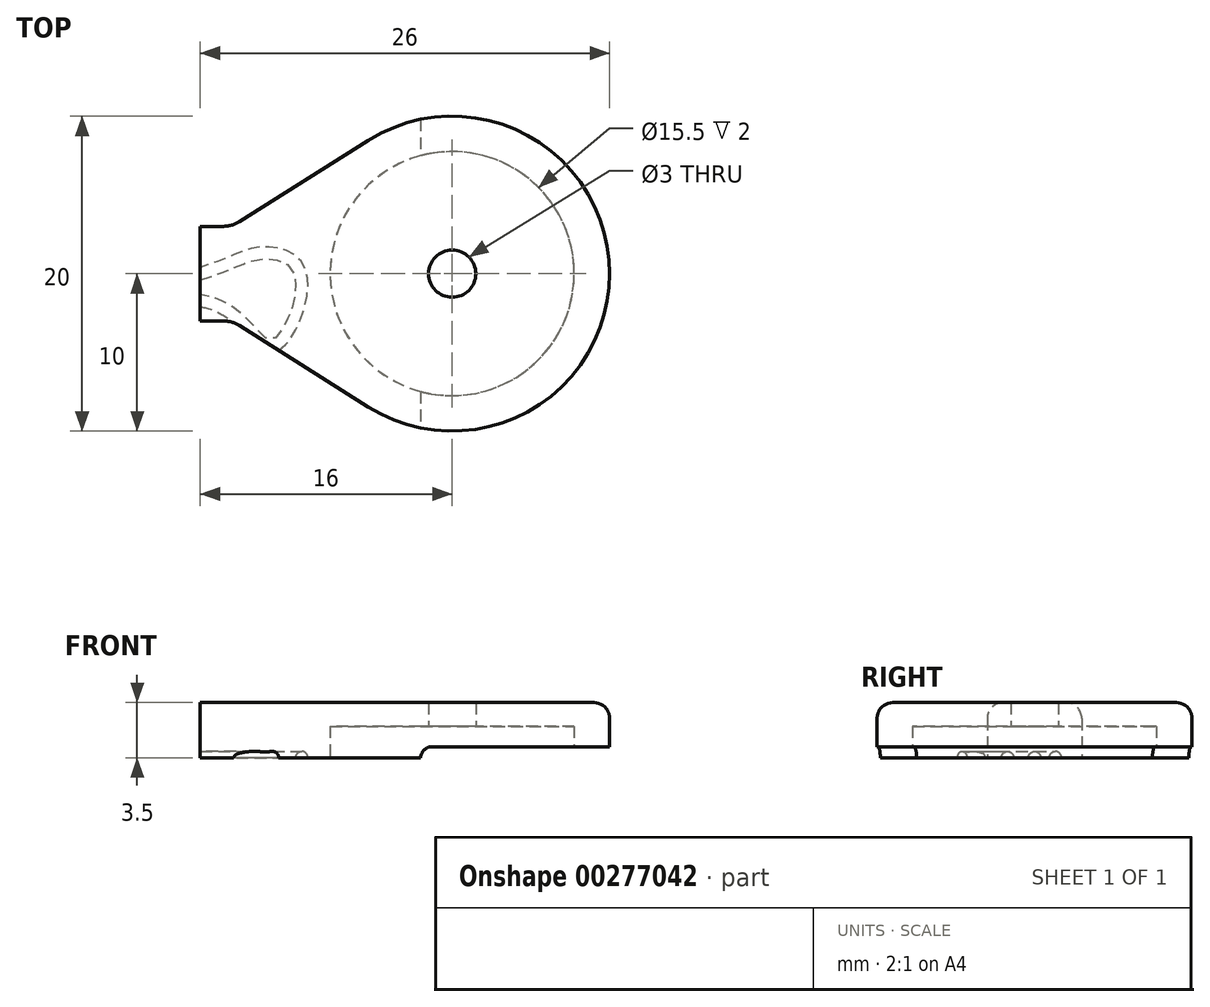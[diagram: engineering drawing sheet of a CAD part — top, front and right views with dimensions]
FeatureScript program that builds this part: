
annotation { "Feature Type Name" : "Feature", "Feature Type Description" : "" }
export const myFeature = defineFeature(function(context is Context, id is Id, definition is map)
    precondition{}
    {
        {
            var Q0;
            Q0=qCreatedBy(makeId("Top.planeOp"),FACE);
            var sketch = newSketch(context, id + "F0", { "sketchPlane" : qUnion([Q0])});
            skCircle(sketch, "E0", {"center": v(0, 0) * mm, "radius": 7.75 * mm});
            skCircle(sketch, "E1", {"center": v(0, 0) * mm, "radius": 10 * mm});
            skSolve(sketch);
        }
        {
            var Q0;
            Q0=qSketchRegion(id+"F0",true);
            extrude(context, id + "F1", {"entities" : qUnion([Q0]), "depth" : 2 * mm});
        }
        {
            var Q0;
            Q0=qCreatedBy(makeId("Top.planeOp"),FACE);
            var sketch = newSketch(context, id + "F2", { "sketchPlane" : qUnion([Q0])});
            skCircle(sketch, "E2.0", {"center": v(0, 0) * mm, "radius": 10 * mm});
            skCircle(sketch, "E3", {"center": v(0, 0) * mm, "radius": 1.5 * mm});
            skSolve(sketch);
        }
        {
            var Q0;
            Q0=qSketchRegion(id+"F2",true);
            extrude(context, id + "F3", {"entities" : qUnion([Q0]), "operationType" : NewBodyOperationType.ADD, "oppositeDirection" : true, "depth" : 1.5 * mm});
        }
        {
            var Q0;
            Q0=qCreatedBy(makeId("Top.planeOp"),FACE);
            var sketch = newSketch(context, id + "F4", { "sketchPlane" : qUnion([Q0])});
            skArc(sketch, "E4.0", {"start": v(-5.33, 8.46) * mm, "mid": v(-10, 0) * mm, "end": v(-5.33, -8.46) * mm});
            skLineSegment(sketch, "E5", {"start": v(-13.51, 3.3) * mm, "end": v(-5.33, 8.46) * mm});
            skLineSegment(sketch, "E6", {"start": v(-13.51, -3.3) * mm, "end": v(-5.33, -8.46) * mm});
            skLineSegment(sketch, "E7.bottom", {"start": v(-14.58, 3) * mm, "end": v(-16, 3) * mm});
            skLineSegment(sketch, "E7.top", {"start": v(-14.58, -3) * mm, "end": v(-16, -3) * mm});
            skLineSegment(sketch, "E7.right", {"start": v(-16, 3) * mm, "end": v(-16, -3) * mm});
            skPoint(sketch, "E8.orphan", {"position": v(-18.76, 0) * mm});
            skPoint(sketch, "E9.visualSharp", {"position": v(-14, 3) * mm});
            skArc(sketch, "E9.filletArc", {"start": v(-14.58, 3) * mm, "mid": v(-14.02, 3.08) * mm, "end": v(-13.51, 3.3) * mm});
            skPoint(sketch, "E10.visualSharp", {"position": v(-14, -3) * mm});
            skArc(sketch, "E10.filletArc", {"start": v(-13.51, -3.3) * mm, "mid": v(-14.02, -3.08) * mm, "end": v(-14.58, -3) * mm});
            skSolve(sketch);
        }
        {
            var Q0;
            Q0=qSketchRegion(id+"F4",true);
            var Q1;
            Q1=makeQuery(id+"F1.opExtrude","CAP_FACE",FACE,{"disambiguationData":[OSD([sQuery(id+"F0.wireOp",EDGE,"E0"),sQuery(id+"F0.wireOp",EDGE,"E1")])],"isStart":false});
            var Q2;
            Q2=makeQuery(id+"F3.opExtrude","CAP_FACE",FACE,{"disambiguationData":[OSD([sQuery(id+"F2.wireOp",EDGE,"E2.0"),sQuery(id+"F2.wireOp",EDGE,"E3")])],"isStart":false});
            extrude(context, id + "F5", {"entities" : qUnion([Q0]), "operationType" : NewBodyOperationType.ADD, "endBound" : BoundingType.UP_TO_SURFACE, "endBoundEntityFace" : qUnion([Q1]), "depth" : 25 * mm, "hasSecondDirection" : true, "secondDirectionBound" : BoundingType.UP_TO_SURFACE, "secondDirectionOppositeDirection" : true, "secondDirectionBoundEntityFace" : qUnion([Q2]), "secondDirectionDepth" : 25 * mm});
        }
        {
            var Q0;
            Q0=qCreatedBy(makeId("Front.planeOp"),FACE);
            var sketch = newSketch(context, id + "F6", { "sketchPlane" : qUnion([Q0])});
            skLineSegment(sketch, "E11", {"start": v(10.19, 2) * mm, "end": v(10.19, 1.3) * mm});
            skLineSegment(sketch, "E12", {"start": v(10.19, 1.3) * mm, "end": v(-1.3, 1.3) * mm});
            skArc(sketch, "E13", {"start": v(-1.3, 1.3) * mm, "mid": v(-1.8, 1.5) * mm, "end": v(-2, 2) * mm});
            skLineSegment(sketch, "E14", {"start": v(-2, 2) * mm, "end": v(10.19, 2) * mm});
            skSolve(sketch);
        }
        {
            var Q0;
            Q0=qSketchRegion(id+"F6",true);
            extrude(context, id + "F7", {"entities" : qUnion([Q0]), "operationType" : NewBodyOperationType.REMOVE, "oppositeDirection" : true, "depth" : 25 * mm, "hasSecondDirection" : true, "secondDirectionOppositeDirection" : false, "secondDirectionDepth" : 25 * mm});
        }
        {
            var Q0;
            {var subQ0=sQuery(id+"F0.wireOp",EDGE,"E1");var subQ1=sQuery(id+"F0.wireOp",EDGE,"E0");Q0=makeQuery(id+"F5.boolean.opBoolean","MERGE",FACE,{"derivedFrom":[makeQuery(id+"F1.opExtrude","CAP_FACE",FACE,{"disambiguationData":[OSD([subQ1,subQ0])],"isStart":false}),makeQuery(id+"F5.opExtrude","CAP_FACE",FACE,{"disambiguationData":[OSD([subQ1,subQ0])],"isStart":false})]});}
            var sketch = newSketch(context, id + "F8", { "sketchPlane" : qUnion([Q0])});
            skFitSpline(sketch, "E15", {"points": [v(-17.04, -0.28) * mm, v(-12.13, 1.31) * mm, v(-9.63, 0) * mm, v(-11.42, -4.62) * mm, v(-16.73, -1.68) * mm], "startDerivative": vector(32.92, 8.05) * mm, "endDerivative": vector(-35.55, -0.33) * mm});
            skSolve(sketch);
        }
        {
            var Q0;
            Q0=makeQuery(id+"F5.opExtrude","SWEPT_FACE",FACE,{"disambiguationData":[OSD([sQuery(id+"F4.wireOp",EDGE,"E7.right")])]});
            var sketch = newSketch(context, id + "F9", { "sketchPlane" : qUnion([Q0])});
            skCircle(sketch, "E16", {"center": v(0, 2) * mm, "radius": 0.4 * mm});
            skPoint(sketch, "E16.centerSnap0", {"position": v(0, 2) * mm});
            skSolve(sketch);
        }
        {
            var Q0;
            Q0=makeQuery(id+"F9.imprint","IMPRINT",FACE,{"disambiguationData":[TD([[makeQuery(id+"F9.imprint","IMPRINT",EDGE,{"derivedFrom":sQuery(id+"F9.wireOp",EDGE,"E16")}),1.0]])]});
            var Q1;
            Q1=qConstructionFilter(qBodyType(qCreatedBy(id+"F8",EDGE),BodyType.WIRE),ConstructionObject.NO);
            sweep(context, id + "F10", {"operationType" : NewBodyOperationType.REMOVE, "profiles" : qUnion([Q0]), "path" : qUnion([Q1])});
        }
        {
            var Q0;
            Q0=makeQuery(id+"F3.opExtrude","CAP_EDGE",EDGE,{"disambiguationData":[OSD([sQuery(id+"F2.wireOp",EDGE,"E2.0")])],"isStart":false});
            var Q1;
            Q1=makeQuery(id+"F5.opExtrude","TWEAK_EDGE",EDGE,{"derivedFrom":[makeQuery(id+"F3.opExtrude","CAP_FACE",FACE,{"disambiguationData":[OSD([sQuery(id+"F2.wireOp",EDGE,"E2.0"),sQuery(id+"F2.wireOp",EDGE,"E3")])],"isStart":false}),makeQuery(id+"F4.imprint","IMPRINT",EDGE,{"derivedFrom":sQuery(id+"F4.wireOp",EDGE,"E7.right")})]});
            fillet(context, id + "F11", {"entities" : qUnion([Q0, Q1]), "radius" : 1 * mm, "tangentPropagation" : true, "allowEdgeOverflow" : false});
        }
        {
            var Q0;
            Q0=makeQuery(id+"F1.opExtrude","SWEPT_BODY",BODY,{"disambiguationData":[OSD([sQuery(id+"F0.wireOp",EDGE,"E0"),sQuery(id+"F0.wireOp",EDGE,"E1")])]});
            var Q1;
            {var subQ1=sQuery(id+"F0.wireOp",EDGE,"E0");var subQ2=sQuery(id+"F0.wireOp",EDGE,"E1");Q1=makeQuery(id+"F10.boolean.opBoolean","SPLIT",FACE,{"disambiguationData":[TD([makeQuery(id+"F1.opExtrude","SWEPT_FACE",FACE,{"disambiguationData":[OSD([subQ1])]})])],"derivedFrom":makeQuery(id+"F5.boolean.opBoolean","MERGE",FACE,{"derivedFrom":[makeQuery(id+"F1.opExtrude","CAP_FACE",FACE,{"disambiguationData":[OSD([subQ1,subQ2])],"isStart":false}),makeQuery(id+"F5.opExtrude","CAP_FACE",FACE,{"disambiguationData":[OSD([subQ1,subQ2])],"isStart":false})]})});}
            mirror(context, id + "F12", {"operationType" : NewBodyOperationType.ADD, "entities" : qUnion([Q0]), "mirrorPlane" : qUnion([Q1])});
        }
        {
            var Q0;
            Q0=qCreatedBy(makeId("Front.planeOp"),FACE);
            var sketch = newSketch(context, id + "F13", { "sketchPlane" : qUnion([Q0])});
            skLineSegment(sketch, "E17", {"start": v(-16, 2) * mm, "end": v(10, 2) * mm});
            skLineSegment(sketch, "E18", {"start": v(-16, 2) * mm, "end": v(-16, -1.5) * mm});
            skLineSegment(sketch, "E19", {"start": v(-16, -1.5) * mm, "end": v(10, -1.5) * mm});
            skLineSegment(sketch, "E20", {"start": v(10, -1.5) * mm, "end": v(10, 2) * mm});
            skSolve(sketch);
        }
        {
            var Q0;
            Q0 = qSketchRegion(id + "F13", true);
            extrude(context, id + "F14", {"entities" : qUnion([Q0]), "operationType" : NewBodyOperationType.REMOVE, "oppositeDirection" : true, "depth" : 25 * mm, "symmetric" : true});
        }
    });
